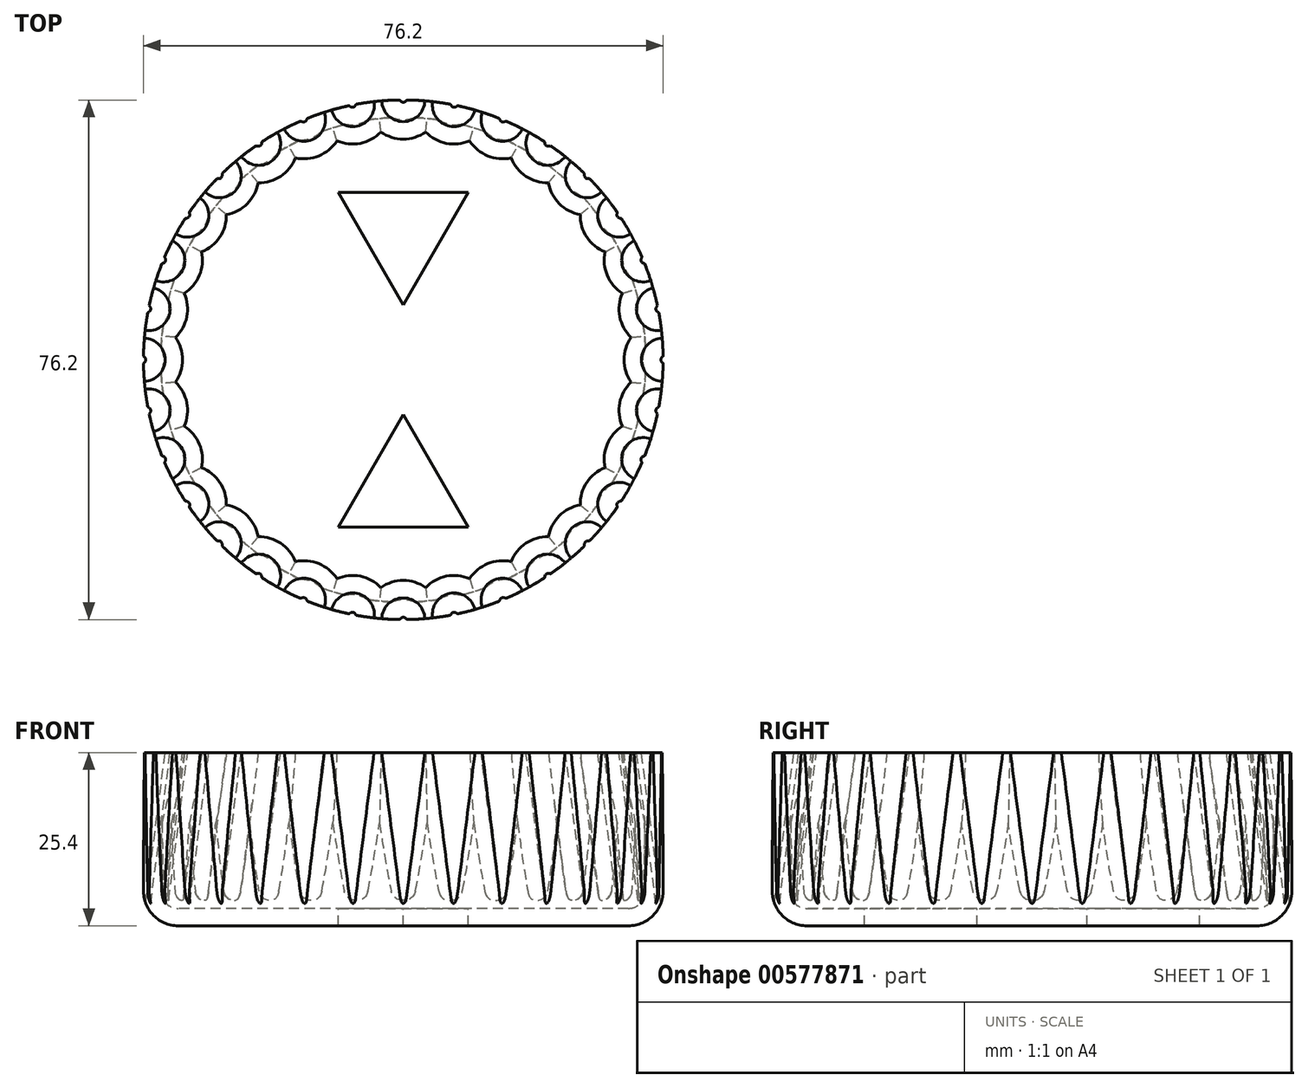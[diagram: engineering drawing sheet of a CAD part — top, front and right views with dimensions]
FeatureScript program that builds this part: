
annotation { "Feature Type Name" : "Feature", "Feature Type Description" : "" }
export const myFeature = defineFeature(function(context is Context, id is Id, definition is map)
    precondition{}
    {
        {
            var Q0;
            Q0=qCreatedBy(makeId("Top.planeOp"),FACE);
            var sketch = newSketch(context, id + "F0", { "sketchPlane" : qUnion([Q0])});
            skCircle(sketch, "E0", {"center": v(0, 0) * mm, "radius": 38.1 * mm});
            skSolve(sketch);
        }
        {
            var Q0;
            Q0 = qSketchRegion(id + "F0", true);
            extrude(context, id + "F1", {"entities" : qUnion([Q0]), "depth" : 25.4 * mm, "offsetDistance" : 25.4 * mm});
        }
        {
            var Q0;
            Q0=makeQuery(id+"F1.opExtrude","CAP_FACE",FACE,{"disambiguationData":[OSD([sQuery(id+"F0.wireOp",EDGE,"E0")])],"isStart":false});
            var sketch = newSketch(context, id + "F2", { "sketchPlane" : qUnion([Q0])});
            skCircle(sketch, "E1", {"center": v(0, 38.1) * mm, "radius": 3.18 * mm});
            skCircle(sketch, "E2.1.0", {"center": v(-7.43, 37.37) * mm, "radius": 3.18 * mm});
            skCircle(sketch, "E2.2.0", {"center": v(-14.58, 35.2) * mm, "radius": 3.18 * mm});
            skCircle(sketch, "E2.3.0", {"center": v(-21.17, 31.68) * mm, "radius": 3.18 * mm});
            skCircle(sketch, "E2.4.0", {"center": v(-26.94, 26.94) * mm, "radius": 3.18 * mm});
            skCircle(sketch, "E2.5.0", {"center": v(-31.68, 21.17) * mm, "radius": 3.18 * mm});
            skCircle(sketch, "E2.6.0", {"center": v(-35.2, 14.58) * mm, "radius": 3.18 * mm});
            skCircle(sketch, "E2.7.0", {"center": v(-37.37, 7.43) * mm, "radius": 3.18 * mm});
            skCircle(sketch, "E2.8.0", {"center": v(-38.1, 0) * mm, "radius": 3.18 * mm});
            skCircle(sketch, "E2.9.0", {"center": v(-37.37, -7.43) * mm, "radius": 3.18 * mm});
            skPoint(sketch, "E2.center", {"position": v(0, 0) * mm});
            skCircle(sketch, "E3.1.10.0", {"center": v(-35.2, -14.58) * mm, "radius": 3.18 * mm});
            skCircle(sketch, "E4.1.11.0", {"center": v(-31.68, -21.17) * mm, "radius": 3.18 * mm});
            skCircle(sketch, "E5.1.12.0", {"center": v(-26.94, -26.94) * mm, "radius": 3.18 * mm});
            skCircle(sketch, "E6.1.13.0", {"center": v(-21.17, -31.68) * mm, "radius": 3.18 * mm});
            skCircle(sketch, "E7.1.14.0", {"center": v(-14.58, -35.2) * mm, "radius": 3.18 * mm});
            skCircle(sketch, "E8.1.15.0", {"center": v(-7.43, -37.37) * mm, "radius": 3.18 * mm});
            skCircle(sketch, "E9.1.16.0", {"center": v(0, -38.1) * mm, "radius": 3.18 * mm});
            skCircle(sketch, "E10.1.17.0", {"center": v(7.43, -37.37) * mm, "radius": 3.18 * mm});
            skCircle(sketch, "E11.1.18.0", {"center": v(14.58, -35.2) * mm, "radius": 3.18 * mm});
            skCircle(sketch, "E12.1.19.0", {"center": v(21.17, -31.68) * mm, "radius": 3.18 * mm});
            skCircle(sketch, "E13.1.20.0", {"center": v(26.94, -26.94) * mm, "radius": 3.18 * mm});
            skCircle(sketch, "E14.1.21.0", {"center": v(31.68, -21.17) * mm, "radius": 3.18 * mm});
            skCircle(sketch, "E15.1.22.0", {"center": v(35.2, -14.58) * mm, "radius": 3.18 * mm});
            skCircle(sketch, "E16.1.23.0", {"center": v(37.37, -7.43) * mm, "radius": 3.18 * mm});
            skCircle(sketch, "E17.1.24.0", {"center": v(38.1, 0) * mm, "radius": 3.18 * mm});
            skCircle(sketch, "E18.1.25.0", {"center": v(37.37, 7.43) * mm, "radius": 3.18 * mm});
            skCircle(sketch, "E19.1.26.0", {"center": v(35.2, 14.58) * mm, "radius": 3.18 * mm});
            skCircle(sketch, "E20.1.27.0", {"center": v(31.68, 21.17) * mm, "radius": 3.18 * mm});
            skCircle(sketch, "E21.1.28.0", {"center": v(26.94, 26.94) * mm, "radius": 3.18 * mm});
            skCircle(sketch, "E22.1.29.0", {"center": v(21.17, 31.68) * mm, "radius": 3.18 * mm});
            skCircle(sketch, "E23.1.30.0", {"center": v(14.58, 35.2) * mm, "radius": 3.18 * mm});
            skCircle(sketch, "E24.1.31.0", {"center": v(7.43, 37.37) * mm, "radius": 3.18 * mm});
            skSolve(sketch);
        }
        {
            var Q0;
            Q0 = qSketchRegion(id + "F2", true);
            extrude(context, id + "F3", {"entities" : qUnion([Q0]), "operationType" : NewBodyOperationType.REMOVE, "oppositeDirection" : true, "depth" : 25.4 * mm, "offsetDistance" : 25.4 * mm, "hasDraft" : true, "draftAngle" : 7.3 * degree, "draftPullDirection" : true});
        }
        {
            var Q0;
            Q0=makeQuery(id+"F1.opExtrude","CAP_EDGE",EDGE,{"disambiguationData":[OSD([sQuery(id+"F0.wireOp",EDGE,"E0")])],"isStart":true});
            fillet(context, id + "F4", {"entities" : qUnion([Q0]), "radius" : 5.08 * mm, "tangentPropagation" : true, "allowEdgeOverflow" : false});
        }
        {
            var Q0;
            Q0=makeQuery(id+"F1.opExtrude","CAP_FACE",FACE,{"disambiguationData":[OSD([sQuery(id+"F0.wireOp",EDGE,"E0")])],"isStart":false});
            shell(context, id + "F5", {"entities" : qUnion([Q0]), "thickness" : 2.54 * mm});
        }
        {
            var Q0;
            Q0=makeQuery(id+"F1.opExtrude","CAP_FACE",FACE,{"disambiguationData":[OSD([sQuery(id+"F0.wireOp",EDGE,"E0")])],"isStart":false});
            var sketch = newSketch(context, id + "F6", { "sketchPlane" : qUnion([Q0])});
            skLineSegment(sketch, "E25", {"start": v(-34.92, 0) * mm, "end": v(34.92, 0) * mm, "construction": true});
            skCircle(sketch, "E26.cCircle", {"center": v(0, 19.05) * mm, "radius": 5.5 * mm, "construction": true});
            skLineSegment(sketch, "E26.0", {"start": v(9.52, 24.55) * mm, "end": v(0, 8.05) * mm});
            skLineSegment(sketch, "E26.1", {"start": v(0, 8.05) * mm, "end": v(-9.53, 24.55) * mm});
            skLineSegment(sketch, "E26.2", {"start": v(-9.53, 24.55) * mm, "end": v(9.52, 24.55) * mm});
            skPoint(sketch, "E26.0.midPoint", {"position": v(4.76, 16.3) * mm});
            skLineSegment(sketch, "E27.MirrorCS", {"start": v(-9.53, -24.55) * mm, "end": v(9.52, -24.55) * mm});
            skLineSegment(sketch, "E28.MirrorCS", {"start": v(9.52, -24.55) * mm, "end": v(0, -8.05) * mm});
            skLineSegment(sketch, "E29.MirrorCS", {"start": v(0, -8.05) * mm, "end": v(-9.53, -24.55) * mm});
            skSolve(sketch);
        }
        {
            var Q0;
            Q0 = qSketchRegion(id + "F6", true);
            extrude(context, id + "F7", {"entities" : qUnion([Q0]), "operationType" : NewBodyOperationType.REMOVE, "oppositeDirection" : true, "depth" : 25.4 * mm, "offsetDistance" : 25.4 * mm});
        }
    });
